# Revit family: EL-AS1247xxWSxxxMRM0350
name_source: partatom
category: Leuchten
units: mm (PartAtom-declared; Revit-internal decimal feet)

## family parameters
Basisbauteil = Fläche
Beim Laden mit Abzugskörper schneiden = Nein
Bemaßung runder Anschluss = Durchmesser verwenden
Gemeinsam genutzt = Nein
Lichtquelle = Ja
OmniClass-Nummer = 23.80.70.11
OmniClass-Titel = Luminaries for Internal Lighting
Raumberechnungspunkt = Nein
Teiletyp = Normal

## types (4) — shared parameters
Baugruppenkennzeichen = D5020200
Datei für fotometrisches Netz = EL-xxx_MRM.IES
Emissionsform beim Rendern sichtbar = Nein
Farbfilter = 16777215
Farbtemperaturverschiebung bei Dämpfen der Lampe = <Keine Auswahl>
Hersteller = RIDI Leuchten GmbH
Lampe = LED
Neigungswinkel = 90.00°
Scheinlast = 30 VA
URL = www.ridi.de
Von Breite des Rechtecks ausssenden = 48 mm  [stored 0.15748 ft]
Von Länge des Rechtecks aussenden = 709 mm  [stored 2.32612 ft]
brand = RIDI
conformity mark = CE
electrical safety class = 1
height = 60 mm  [stored 0.19685 ft]
ingress protection (IP) code = IP40
length = 1255 mm  [stored 4.11745 ft]
nominal frequency = 50-60Hz
nominal voltage = 230
rated input power = 30
voltage type (AC, DC, UC) = AC
weight = 5,1 kg
width = 187 mm  [stored 0.613517 ft]
zero-valued in all types: Vorgabe-Ansicht

## per-type parameters (varying)
| type | Modell |
| EL-AS1247NDWS830MRM0350 | 0627647 |
| EL-AS1247DAWS830MRM0350 | 0637647 |
| EL-AS1247NDWS840MRM0350 | 0627648 |
| EL-AS1247DAWS840MRM0350 | 0637648 |

note: column(s) folded — value = type name in every type: product name

note: [stored X ft] marks values corroborated as IEEE doubles in the binary element streams (Revit-internal decimal feet)
